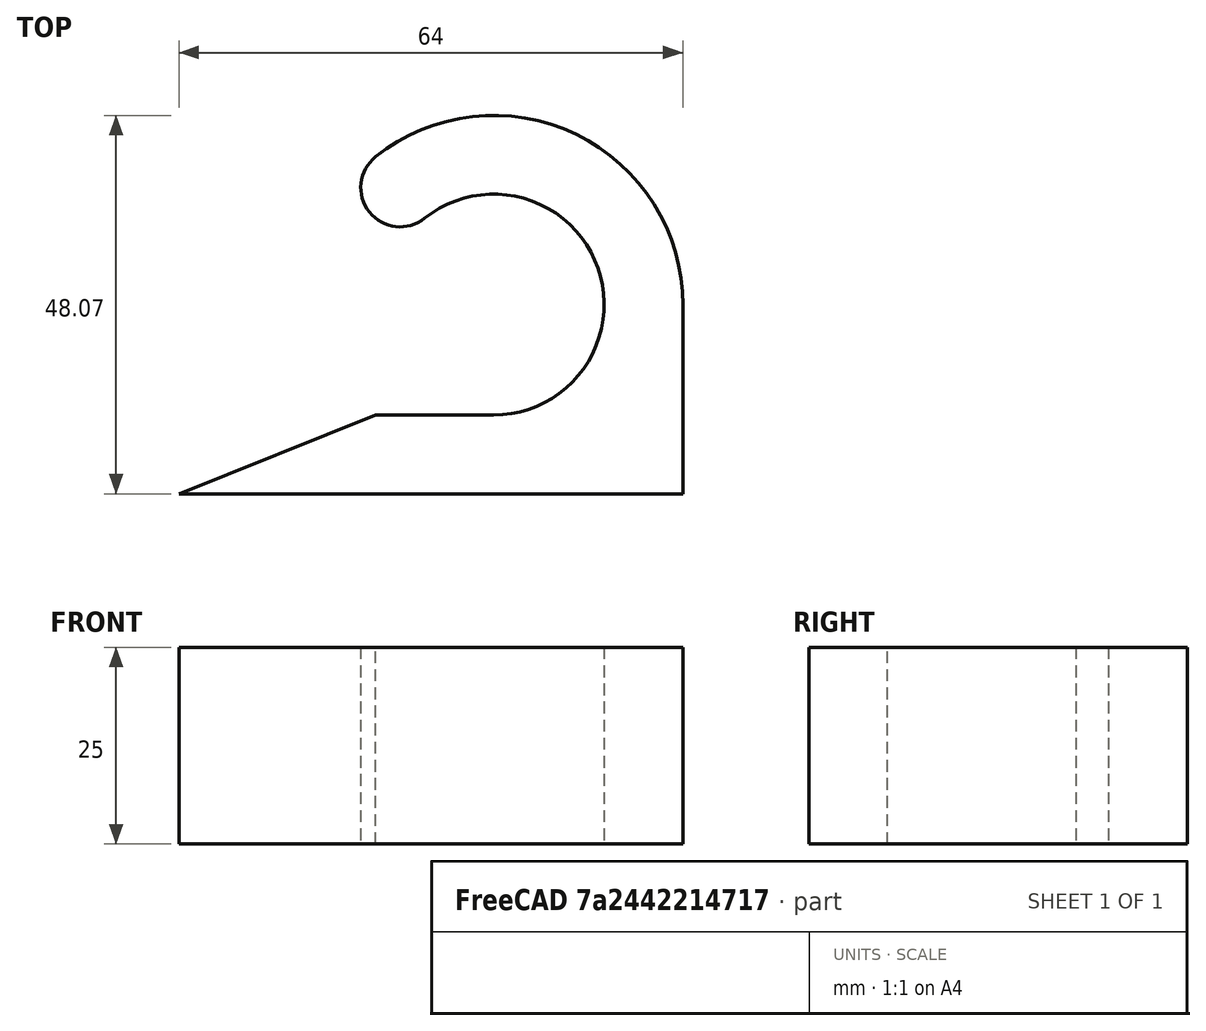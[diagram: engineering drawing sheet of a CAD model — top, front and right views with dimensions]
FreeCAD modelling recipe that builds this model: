
FCSTD DOCUMENT  (FreeCAD 0.19R22262 (Git))
Label: haken_kukuto
License: All rights reserved
LicenseURL: http://en.wikipedia.org/wiki/All_rights_reserved
objects: Sketcher::SketchObject×1, PartDesign::Pad×1, PartDesign::Body×1
note: 4 computed .brp shape members not serialized (recipe doc carries the construction recipe); baked Part::Feature solids carry a one-line shape summary decoded from their .brp

FEATURE [Sketcher::SketchObject] Sketch
  MapMode = 5
  Support = -> [XY_Plane]
  sketch-geometry (7):
    g0: ArcOfCircle CenterX=39.9656 CenterY=24.0344 CenterZ=0 NormalX=0 NormalY=0 NormalZ=1 AngleXU=0 Radius=24.0344 StartAngle=6.28175 EndAngle=8.52797
    g1: ArcOfCircle CenterX=28.0862 CenterY=38.9067 CenterZ=0 NormalX=0 NormalY=0 NormalZ=1 AngleXU=0 Radius=5 StartAngle=2.24478 EndAngle=5.38638
    g2: ArcOfCircle CenterX=39.9656 CenterY=24.0344 CenterZ=0 NormalX=0 NormalY=0 NormalZ=1 AngleXU=0 Radius=14.0344 StartAngle=4.71233 EndAngle=8.52797
    g3: LineSegment StartX=39.9648 StartY=10 StartZ=0 EndX=24.9656 EndY=10 EndZ=0
    g4: LineSegment StartX=24.9656 StartY=10 StartZ=0 EndX=0 EndY=0 EndZ=0
    g5: LineSegment StartX=64 StartY=0 StartZ=0 EndX=64 EndY=24 EndZ=0
    g6: LineSegment StartX=0 StartY=0 StartZ=0 EndX=64 EndY=0 EndZ=0
  constraints (20):
    c: Tangent(g0,g1) = -1.5708
    c: Tangent(g1,g2) = 1.5708
    c: Coincident(g2,g3)
    c: Horizontal(g3)
    c: Coincident(g3,g4)
    c: Coincident(g0,g2)
    c: DistanceY(g4,g3) = 10
    c: DistanceY(g2,g1) = 25
    c: DistanceX(g0,g0) = 15
    c: Vertical(g3,g0)
    c: PointOnObject(g5,g-1)
    c: Vertical(g5)
    c: Coincident(g0,g5)
    c: Coincident(g6,g4)
    c: Coincident(g6,g5)
    c: DistanceX(g6,g6) = 64
    c: DistanceY(g5,g5) = 24
    c: Coincident(g-1,g4)
    c: Distance(g0,g1) = 10
    c: Angle(g2) = 3.81564
FEATURE [PartDesign::Pad] Pad
  AllowMultiFace = false
  Length = 25
  Length2 = 100
  Profile = -> Sketch
  Refine = true
  Type = 0
FEATURE [PartDesign::Body] Body
  Group = -> [Sketch,Pad]
  Origin = -> Origin
  Tip = -> Pad
